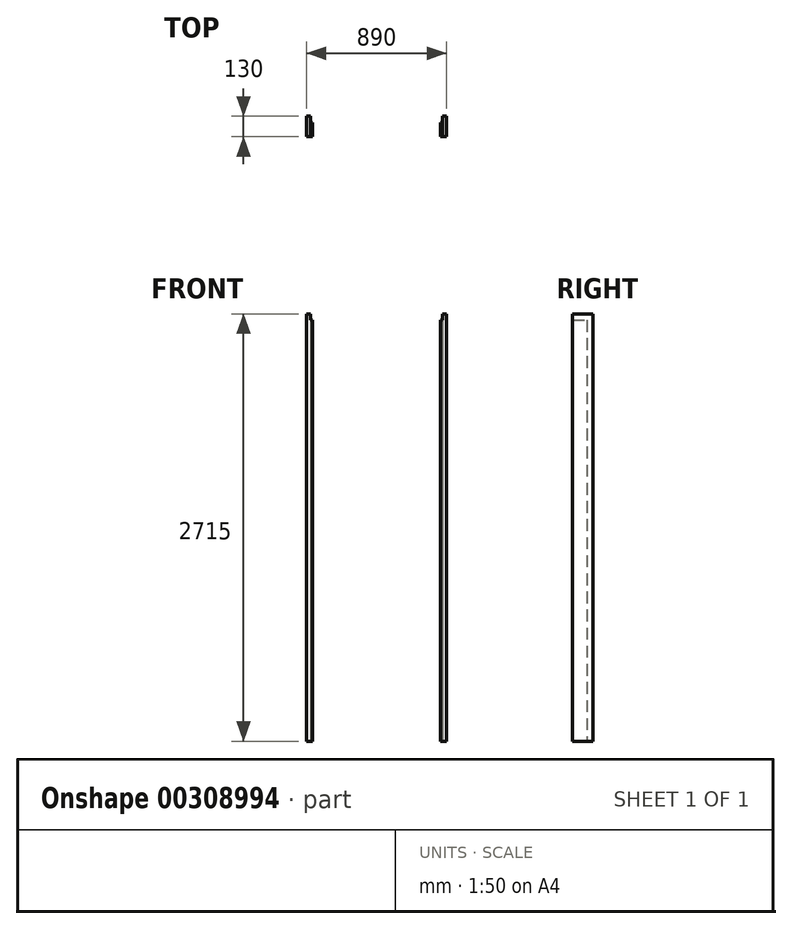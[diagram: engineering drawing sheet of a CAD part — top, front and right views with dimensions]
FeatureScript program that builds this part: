
annotation { "Feature Type Name" : "Feature", "Feature Type Description" : "" }
export const myFeature = defineFeature(function(context is Context, id is Id, definition is map)
    precondition{}
    {
        {
            var Q0;
            Q0=qCreatedBy(makeId("Top.planeOp"),FACE);
            var sketch = newSketch(context, id + "F0", { "sketchPlane" : qUnion([Q0])});
            skLineSegment(sketch, "E0.bottom", {"start": v(-445, 40) * mm, "end": v(-419, 40) * mm});
            skLineSegment(sketch, "E0.top", {"start": v(-445, -90) * mm, "end": v(-406, -90) * mm});
            skLineSegment(sketch, "E0.left", {"start": v(-445, 40) * mm, "end": v(-445, -90) * mm});
            skLineSegment(sketch, "E0.right", {"start": v(-406, 0) * mm, "end": v(-406, -90) * mm});
            skPoint(sketch, "E1.oppositeSnap0", {"position": v(-406, 0) * mm});
            skLineSegment(sketch, "E1.top", {"start": v(-419, 0) * mm, "end": v(-406, 0) * mm});
            skLineSegment(sketch, "E1.left", {"start": v(-419, 40) * mm, "end": v(-419, 0) * mm});
            skLineSegment(sketch, "E2.bottom", {"start": v(419, 40) * mm, "end": v(445, 40) * mm});
            skLineSegment(sketch, "E2.top", {"start": v(406, -90) * mm, "end": v(445, -90) * mm});
            skLineSegment(sketch, "E2.left", {"start": v(406, 0) * mm, "end": v(406, -90) * mm});
            skLineSegment(sketch, "E2.right", {"start": v(445, 40) * mm, "end": v(445, -90) * mm});
            skLineSegment(sketch, "E3.top", {"start": v(406, 0) * mm, "end": v(419, 0) * mm});
            skLineSegment(sketch, "E3.right", {"start": v(419, 40) * mm, "end": v(419, 0) * mm});
            skLineSegment(sketch, "E4", {"start": v(-406, 0) * mm, "end": v(406, 0) * mm, "construction": true});
            skSolve(sketch);
        }
        {
            var Q0;
            Q0 = qSketchRegion(id + "F0", true);
            extrude(context, id + "F1", {"entities" : qUnion([Q0]), "depth" : 2715 * mm});
        }
        {
            var Q0;
            Q0=makeQuery(id+"F1.opExtrude","SWEPT_FACE",FACE,{"disambiguationData":[OSD([sQuery(id+"F0.wireOp",EDGE,"E0.top")])]});
            var sketch = newSketch(context, id + "F2", { "sketchPlane" : qUnion([Q0])});
            skLineSegment(sketch, "E5.bottom", {"start": v(-419, 2715) * mm, "end": v(419, 2715) * mm});
            skLineSegment(sketch, "E5.top", {"start": v(-419, 2676) * mm, "end": v(419, 2676) * mm});
            skLineSegment(sketch, "E5.left", {"start": v(-419, 2715) * mm, "end": v(-419, 2676) * mm});
            skLineSegment(sketch, "E5.right", {"start": v(419, 2715) * mm, "end": v(419, 2676) * mm});
            skLineSegment(sketch, "E6", {"start": v(0, 0) * mm, "end": v(0, 2676) * mm, "construction": true});
            skSolve(sketch);
        }
        {
            var Q0;
            Q0 = qSketchRegion(id + "F2", true);
            extrude(context, id + "F3", {"entities" : qUnion([Q0]), "operationType" : NewBodyOperationType.REMOVE, "oppositeDirection" : true, "depth" : 130 * mm});
        }
    });
